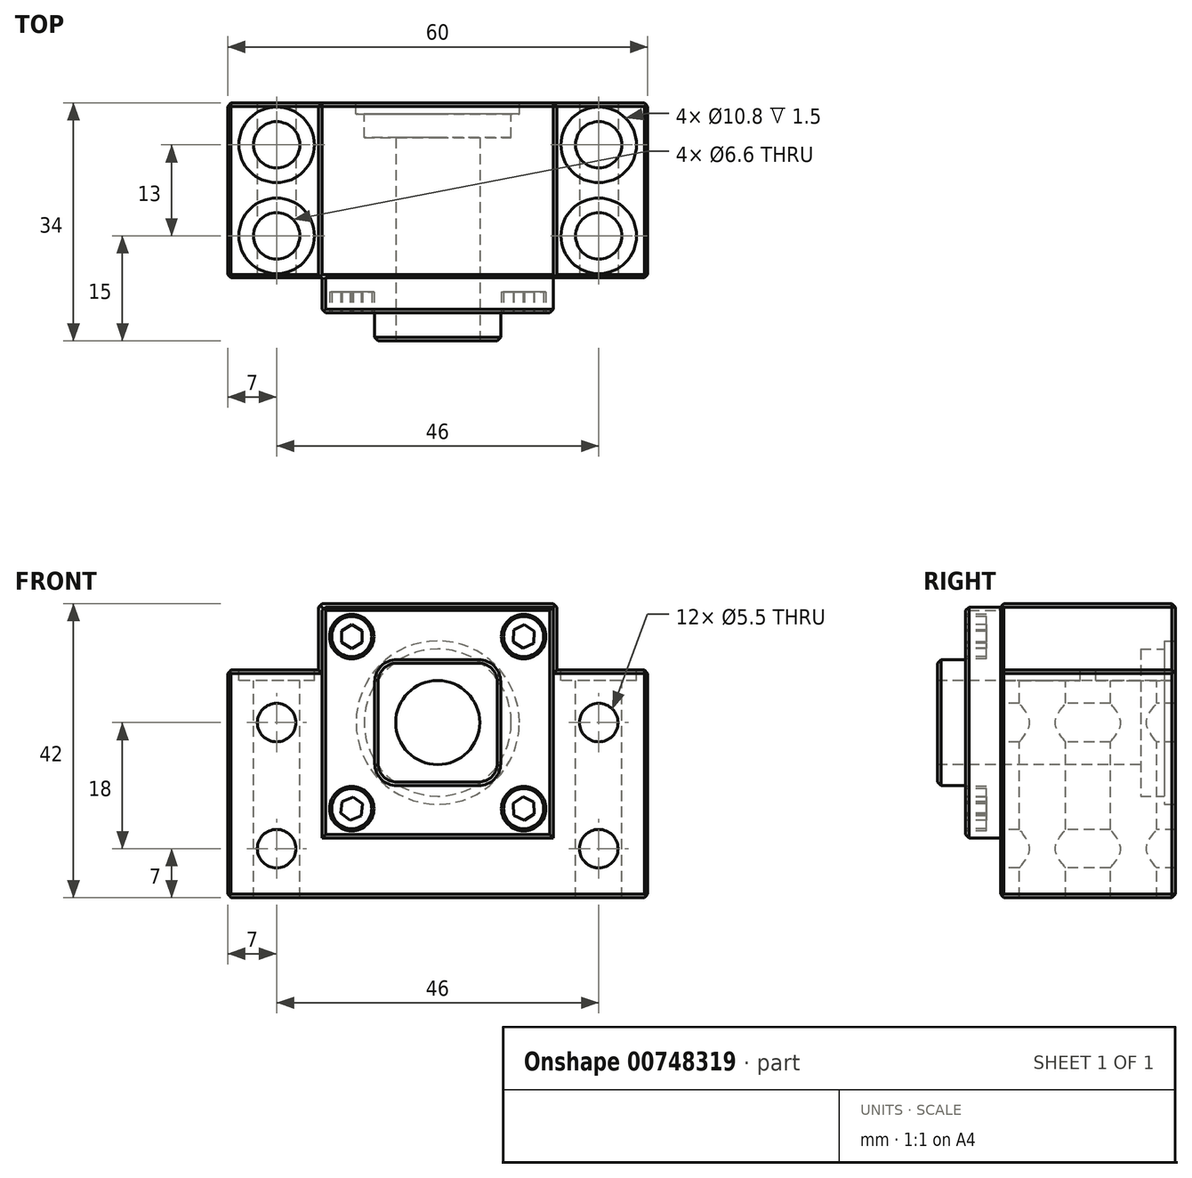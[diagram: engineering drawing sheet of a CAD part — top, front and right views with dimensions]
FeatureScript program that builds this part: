
annotation { "Feature Type Name" : "Feature", "Feature Type Description" : "" }
export const myFeature = defineFeature(function(context is Context, id is Id, definition is map)
    precondition{}
    {
        {
            var Q0;
            Q0=qCreatedBy(makeId("Front.planeOp"),FACE);
            var sketch = newSketch(context, id + "F0", { "sketchPlane" : qUnion([Q0])});
            skLineSegment(sketch, "E0.bottom", {"start": v(0, 0) * mm, "end": v(60, 0) * mm});
            skLineSegment(sketch, "E0.top", {"start": v(0, 32.5) * mm, "end": v(13, 32.5) * mm});
            skLineSegment(sketch, "E0.left", {"start": v(0, 0) * mm, "end": v(0, 32.5) * mm});
            skLineSegment(sketch, "E0.right", {"start": v(60, 0) * mm, "end": v(60, 32.5) * mm});
            skLineSegment(sketch, "E1", {"start": v(30, 32.5) * mm, "end": v(30, 0) * mm, "construction": true});
            skLineSegment(sketch, "E2", {"start": v(0, 25) * mm, "end": v(60, 25) * mm, "construction": true});
            skLineSegment(sketch, "E3.bottom", {"start": v(47, 42) * mm, "end": v(13, 42) * mm});
            skLineSegment(sketch, "E3.left", {"start": v(47, 42) * mm, "end": v(47, 32.5) * mm});
            skLineSegment(sketch, "E3.right", {"start": v(13, 42) * mm, "end": v(13, 32.5) * mm});
            skPoint(sketch, "E3.middle", {"position": v(30, 25) * mm});
            skLineSegment(sketch, "E4.trimOffspring", {"start": v(47, 32.5) * mm, "end": v(60, 32.5) * mm});
            skSolve(sketch);
        }
        {
            var Q0;
            Q0 = qSketchRegion(id + "F0", true);
            extrude(context, id + "F1", {"entities" : qUnion([Q0]), "depth" : 25 * mm, "offsetDistance" : 25.4 * mm});
        }
        {
            var Q0;
            Q0=makeQuery(id+"F1.opExtrude","CAP_FACE",FACE,{"disambiguationData":[OSD([sQuery(id+"F0.wireOp",EDGE,"E0.bottom"),sQuery(id+"F0.wireOp",EDGE,"E0.top"),sQuery(id+"F0.wireOp",EDGE,"E0.left"),sQuery(id+"F0.wireOp",EDGE,"E0.right"),sQuery(id+"F0.wireOp",EDGE,"E3.bottom"),sQuery(id+"F0.wireOp",EDGE,"E3.left"),sQuery(id+"F0.wireOp",EDGE,"E3.right"),sQuery(id+"F0.wireOp",EDGE,"E4.trimOffspring")])],"isStart":false});
            var sketch = newSketch(context, id + "F2", { "sketchPlane" : qUnion([Q0])});
            skLineSegment(sketch, "E5", {"start": v(30, 42) * mm, "end": v(30, 0) * mm, "construction": true});
            skLineSegment(sketch, "E6", {"start": v(0, 25) * mm, "end": v(60, 25) * mm, "construction": true});
            skPoint(sketch, "E7.middle", {"position": v(30, 25) * mm});
            skLineSegment(sketch, "E8.bottom", {"start": v(46.5, 41.5) * mm, "end": v(13.5, 41.5) * mm});
            skLineSegment(sketch, "E8.top", {"start": v(46.5, 8.5) * mm, "end": v(13.5, 8.5) * mm});
            skLineSegment(sketch, "E8.left", {"start": v(46.5, 41.5) * mm, "end": v(46.5, 8.5) * mm});
            skLineSegment(sketch, "E8.right", {"start": v(13.5, 41.5) * mm, "end": v(13.5, 8.5) * mm});
            skSolve(sketch);
        }
        {
            var Q0;
            Q0 = qSketchRegion(id + "F2", true);
            extrude(context, id + "F3", {"entities" : qUnion([Q0]), "operationType" : NewBodyOperationType.ADD, "depth" : 5 * mm, "offsetDistance" : 25.4 * mm});
        }
        {
            var Q0;
            Q0=makeQuery(id+"F3.opExtrude","CAP_FACE",FACE,{"disambiguationData":[OSD([sQuery(id+"F2.wireOp",EDGE,"E8.bottom"),sQuery(id+"F2.wireOp",EDGE,"E8.top"),sQuery(id+"F2.wireOp",EDGE,"E8.left"),sQuery(id+"F2.wireOp",EDGE,"E8.right")])],"isStart":false});
            var sketch = newSketch(context, id + "F4", { "sketchPlane" : qUnion([Q0])});
            skLineSegment(sketch, "E9.bottom", {"start": v(35.83, 34) * mm, "end": v(24.17, 34) * mm});
            skLineSegment(sketch, "E9.top", {"start": v(35.83, 16) * mm, "end": v(24.17, 16) * mm});
            skLineSegment(sketch, "E9.left", {"start": v(39, 30.83) * mm, "end": v(39, 19.17) * mm});
            skLineSegment(sketch, "E9.right", {"start": v(21, 30.83) * mm, "end": v(21, 19.17) * mm});
            skPoint(sketch, "E9.middle", {"position": v(30, 25) * mm});
            skPoint(sketch, "E9.middle.positionSnap0", {"position": v(46.5, 25) * mm});
            skPoint(sketch, "E9.middle.positionSnap1", {"position": v(30, 41.5) * mm});
            skPoint(sketch, "E9.centerSnap0", {"position": v(46.5, 25) * mm});
            skPoint(sketch, "E9.centerSnap1", {"position": v(30, 41.5) * mm});
            skPoint(sketch, "E10.visualSharp", {"position": v(21, 34) * mm});
            skArc(sketch, "E10.filletArc", {"start": v(24.17, 34) * mm, "mid": v(21.93, 33.07) * mm, "end": v(21, 30.83) * mm});
            skPoint(sketch, "E11.visualSharp", {"position": v(39, 34) * mm});
            skArc(sketch, "E11.filletArc", {"start": v(39, 30.83) * mm, "mid": v(38.07, 33.07) * mm, "end": v(35.83, 34) * mm});
            skPoint(sketch, "E12.visualSharp", {"position": v(39, 16) * mm});
            skArc(sketch, "E12.filletArc", {"start": v(35.83, 16) * mm, "mid": v(38.07, 16.93) * mm, "end": v(39, 19.17) * mm});
            skPoint(sketch, "E13.visualSharp", {"position": v(21, 16) * mm});
            skArc(sketch, "E13.filletArc", {"start": v(21, 19.17) * mm, "mid": v(21.93, 16.93) * mm, "end": v(24.17, 16) * mm});
            skSolve(sketch);
        }
        {
            var Q0;
            Q0 = qSketchRegion(id + "F4", true);
            extrude(context, id + "F5", {"entities" : qUnion([Q0]), "operationType" : NewBodyOperationType.ADD, "depth" : 4 * mm, "offsetDistance" : 25.4 * mm});
        }
        {
            var Q0;
            Q0=makeQuery(id+"F5.opExtrude","CAP_FACE",FACE,{"disambiguationData":[OSD([sQuery(id+"F4.wireOp",EDGE,"E9.bottom"),sQuery(id+"F4.wireOp",EDGE,"E9.top"),sQuery(id+"F4.wireOp",EDGE,"E9.left"),sQuery(id+"F4.wireOp",EDGE,"E9.right"),sQuery(id+"F4.wireOp",EDGE,"E10.filletArc"),sQuery(id+"F4.wireOp",EDGE,"E11.filletArc"),sQuery(id+"F4.wireOp",EDGE,"E12.filletArc"),sQuery(id+"F4.wireOp",EDGE,"E13.filletArc")])],"isStart":false});
            var sketch = newSketch(context, id + "F6", { "sketchPlane" : qUnion([Q0])});
            skCircle(sketch, "E14", {"center": v(30, 25) * mm, "radius": 6 * mm});
            skPoint(sketch, "E14.centerSnap0", {"position": v(39, 25) * mm});
            skPoint(sketch, "E14.centerSnap1", {"position": v(30, 34) * mm});
            skSolve(sketch);
        }
        {
            var Q0;
            Q0 = qSketchRegion(id + "F6", true);
            extrude(context, id + "F7", {"entities" : qUnion([Q0]), "operationType" : NewBodyOperationType.REMOVE, "endBound" : BoundingType.THROUGH_ALL, "oppositeDirection" : true, "depth" : 25.4 * mm, "offsetDistance" : 25.4 * mm});
        }
        {
            var Q0;
            Q0=makeQuery(id+"F1.opExtrude","CAP_FACE",FACE,{"disambiguationData":[OSD([sQuery(id+"F0.wireOp",EDGE,"E0.bottom"),sQuery(id+"F0.wireOp",EDGE,"E0.top"),sQuery(id+"F0.wireOp",EDGE,"E0.left"),sQuery(id+"F0.wireOp",EDGE,"E0.right"),sQuery(id+"F0.wireOp",EDGE,"E3.bottom"),sQuery(id+"F0.wireOp",EDGE,"E3.left"),sQuery(id+"F0.wireOp",EDGE,"E3.right"),sQuery(id+"F0.wireOp",EDGE,"E4.trimOffspring")])],"isStart":false});
            var sketch = newSketch(context, id + "F8", { "sketchPlane" : qUnion([Q0])});
            skLineSegment(sketch, "E15", {"start": v(0, 25) * mm, "end": v(60, 25) * mm, "construction": true});
            skLineSegment(sketch, "E16", {"start": v(30, 25) * mm, "end": v(30, 0) * mm, "construction": true});
            skLineSegment(sketch, "E17.0", {"start": v(7, 25) * mm, "end": v(7, 0) * mm, "construction": true});
            skLineSegment(sketch, "E18.0", {"start": v(53, 25) * mm, "end": v(53, 0) * mm, "construction": true});
            skLineSegment(sketch, "E19", {"start": v(7, 7) * mm, "end": v(53, 7) * mm, "construction": true});
            skCircle(sketch, "E20", {"center": v(7, 25) * mm, "radius": 2.75 * mm});
            skCircle(sketch, "E21", {"center": v(7, 7) * mm, "radius": 2.75 * mm});
            skCircle(sketch, "E22", {"center": v(53, 25) * mm, "radius": 2.75 * mm});
            skCircle(sketch, "E23", {"center": v(53, 7) * mm, "radius": 2.75 * mm});
            skSolve(sketch);
        }
        {
            var Q0;
            Q0 = qSketchRegion(id + "F8", true);
            extrude(context, id + "F9", {"entities" : qUnion([Q0]), "operationType" : NewBodyOperationType.REMOVE, "endBound" : BoundingType.THROUGH_ALL, "oppositeDirection" : true, "depth" : 25.4 * mm, "offsetDistance" : 25.4 * mm});
        }
        {
            var Q0;
            Q0=makeQuery(id+"F1.opExtrude","SWEPT_FACE",FACE,{"disambiguationData":[OSD([sQuery(id+"F0.wireOp",EDGE,"E4.trimOffspring")])]});
            var sketch = newSketch(context, id + "F10", { "sketchPlane" : qUnion([Q0])});
            skLineSegment(sketch, "E24", {"start": v(60, -12.5) * mm, "end": v(0, -12.5) * mm, "construction": true});
            skLineSegment(sketch, "E25.0", {"start": v(60, -6) * mm, "end": v(0, -6) * mm, "construction": true});
            skLineSegment(sketch, "E26.0", {"start": v(60, -19) * mm, "end": v(0, -19) * mm, "construction": true});
            skLineSegment(sketch, "E27", {"start": v(30, -6) * mm, "end": v(30, -19) * mm, "construction": true});
            skLineSegment(sketch, "E28.0", {"start": v(7, -6) * mm, "end": v(7, -19) * mm, "construction": true});
            skLineSegment(sketch, "E29.0", {"start": v(53, -6) * mm, "end": v(53, -19) * mm, "construction": true});
            skCircle(sketch, "E30", {"center": v(7, -6) * mm, "radius": 5.4 * mm});
            skCircle(sketch, "E31", {"center": v(7, -19) * mm, "radius": 5.4 * mm});
            skCircle(sketch, "E32", {"center": v(53, -6) * mm, "radius": 5.4 * mm});
            skCircle(sketch, "E33", {"center": v(53, -19) * mm, "radius": 5.4 * mm});
            skSolve(sketch);
        }
        {
            var Q0;
            Q0 = qSketchRegion(id + "F10", true);
            extrude(context, id + "F11", {"entities" : qUnion([Q0]), "operationType" : NewBodyOperationType.REMOVE, "oppositeDirection" : true, "depth" : 1.5 * mm, "offsetDistance" : 25.4 * mm});
        }
        {
            var Q0;
            Q0=makeQuery(id+"F11.boolean.opBoolean","COPY",FACE,{"derivedFrom":makeQuery(id+"F11.opExtrude","CAP_FACE",FACE,{"disambiguationData":[OSD([sQuery(id+"F10.wireOp",EDGE,"E30")])],"isStart":false})});
            var sketch = newSketch(context, id + "F12", { "sketchPlane" : qUnion([Q0])});
            skCircle(sketch, "E34", {"center": v(7, -6) * mm, "radius": 3.3 * mm});
            skLineSegment(sketch, "E35", {"start": v(7, -6) * mm, "end": v(53, -6) * mm, "construction": true});
            skLineSegment(sketch, "E36", {"start": v(53, -6) * mm, "end": v(53, -19) * mm, "construction": true});
            skLineSegment(sketch, "E37", {"start": v(53, -19) * mm, "end": v(7, -19) * mm, "construction": true});
            skCircle(sketch, "E38", {"center": v(53, -6) * mm, "radius": 3.3 * mm});
            skCircle(sketch, "E39", {"center": v(53, -19) * mm, "radius": 3.3 * mm});
            skCircle(sketch, "E40", {"center": v(7, -19) * mm, "radius": 3.3 * mm});
            skSolve(sketch);
        }
        {
            var Q0;
            Q0 = qSketchRegion(id + "F12", true);
            extrude(context, id + "F13", {"entities" : qUnion([Q0]), "operationType" : NewBodyOperationType.REMOVE, "endBound" : BoundingType.THROUGH_ALL, "oppositeDirection" : true, "depth" : 25.4 * mm, "offsetDistance" : 25.4 * mm});
        }
        {
            var Q0;
            Q0=makeQuery(id+"F3.opExtrude","CAP_FACE",FACE,{"disambiguationData":[OSD([sQuery(id+"F2.wireOp",EDGE,"E8.bottom"),sQuery(id+"F2.wireOp",EDGE,"E8.top"),sQuery(id+"F2.wireOp",EDGE,"E8.left"),sQuery(id+"F2.wireOp",EDGE,"E8.right")])],"isStart":false});
            var sketch = newSketch(context, id + "F14", { "sketchPlane" : qUnion([Q0])});
            skLineSegment(sketch, "E41", {"start": v(21.93, 33.07) * mm, "end": v(13.5, 41.5) * mm, "construction": true});
            skLineSegment(sketch, "E42", {"start": v(38.07, 33.07) * mm, "end": v(46.5, 41.5) * mm, "construction": true});
            skLineSegment(sketch, "E43", {"start": v(38.07, 16.93) * mm, "end": v(46.5, 8.5) * mm, "construction": true});
            skLineSegment(sketch, "E44", {"start": v(21.93, 16.93) * mm, "end": v(13.5, 8.5) * mm, "construction": true});
            skCircle(sketch, "E45", {"center": v(17.71, 37.29) * mm, "radius": 3.18 * mm});
            skCircle(sketch, "E46", {"center": v(42.29, 37.29) * mm, "radius": 3.18 * mm});
            skCircle(sketch, "E47", {"center": v(42.29, 12.71) * mm, "radius": 3.18 * mm});
            skCircle(sketch, "E48", {"center": v(17.71, 12.71) * mm, "radius": 3.18 * mm});
            skCircle(sketch, "E49", {"center": v(17.71, 37.29) * mm, "radius": 2.86 * mm});
            skCircle(sketch, "E50", {"center": v(42.29, 37.29) * mm, "radius": 2.86 * mm});
            skCircle(sketch, "E51", {"center": v(42.29, 12.71) * mm, "radius": 2.86 * mm});
            skCircle(sketch, "E52", {"center": v(17.71, 12.71) * mm, "radius": 2.86 * mm});
            skLineSegment(sketch, "E53.0", {"start": v(19.18, 38.13) * mm, "end": v(19.18, 36.44) * mm});
            skLineSegment(sketch, "E53.1", {"start": v(19.18, 36.44) * mm, "end": v(17.71, 35.6) * mm});
            skLineSegment(sketch, "E53.2", {"start": v(17.71, 35.6) * mm, "end": v(16.25, 36.44) * mm});
            skLineSegment(sketch, "E53.3", {"start": v(16.25, 36.44) * mm, "end": v(16.25, 38.13) * mm});
            skLineSegment(sketch, "E53.4", {"start": v(16.25, 38.13) * mm, "end": v(17.71, 38.97) * mm});
            skLineSegment(sketch, "E53.5", {"start": v(17.71, 38.97) * mm, "end": v(19.18, 38.13) * mm});
            skPoint(sketch, "E53.0.midPoint", {"position": v(19.18, 37.29) * mm});
            skLineSegment(sketch, "E54.0", {"start": v(43.8, 38.04) * mm, "end": v(43.7, 36.36) * mm});
            skLineSegment(sketch, "E54.1", {"start": v(43.7, 36.36) * mm, "end": v(42.18, 35.6) * mm});
            skLineSegment(sketch, "E54.2", {"start": v(42.18, 35.6) * mm, "end": v(40.78, 36.53) * mm});
            skLineSegment(sketch, "E54.3", {"start": v(40.78, 36.53) * mm, "end": v(40.88, 38.21) * mm});
            skLineSegment(sketch, "E54.4", {"start": v(40.88, 38.21) * mm, "end": v(42.39, 38.97) * mm});
            skLineSegment(sketch, "E54.5", {"start": v(42.39, 38.97) * mm, "end": v(43.8, 38.04) * mm});
            skPoint(sketch, "E54.0.midPoint", {"position": v(43.74, 37.2) * mm});
            skLineSegment(sketch, "E55.0", {"start": v(43.7, 13.64) * mm, "end": v(43.8, 11.96) * mm});
            skLineSegment(sketch, "E55.1", {"start": v(43.8, 11.96) * mm, "end": v(42.39, 11.03) * mm});
            skLineSegment(sketch, "E55.2", {"start": v(42.39, 11.03) * mm, "end": v(40.88, 11.79) * mm});
            skLineSegment(sketch, "E55.3", {"start": v(40.88, 11.79) * mm, "end": v(40.78, 13.47) * mm});
            skLineSegment(sketch, "E55.4", {"start": v(40.78, 13.47) * mm, "end": v(42.18, 14.4) * mm});
            skLineSegment(sketch, "E55.5", {"start": v(42.18, 14.4) * mm, "end": v(43.7, 13.64) * mm});
            skPoint(sketch, "E55.0.midPoint", {"position": v(43.74, 12.8) * mm});
            skLineSegment(sketch, "E56.0", {"start": v(19.26, 13.38) * mm, "end": v(19.07, 11.7) * mm});
            skLineSegment(sketch, "E56.1", {"start": v(19.07, 11.7) * mm, "end": v(17.52, 11.04) * mm});
            skLineSegment(sketch, "E56.2", {"start": v(17.52, 11.04) * mm, "end": v(16.17, 12.05) * mm});
            skLineSegment(sketch, "E56.3", {"start": v(16.17, 12.05) * mm, "end": v(16.36, 13.72) * mm});
            skLineSegment(sketch, "E56.4", {"start": v(16.36, 13.72) * mm, "end": v(17.91, 14.39) * mm});
            skLineSegment(sketch, "E56.5", {"start": v(17.91, 14.39) * mm, "end": v(19.26, 13.38) * mm});
            skPoint(sketch, "E56.0.midPoint", {"position": v(19.17, 12.55) * mm});
            skSolve(sketch);
        }
        {
            var Q0;
            Q0=makeQuery(id+"F14.imprint","IMPRINT",FACE,{"disambiguationData":[TD([[makeQuery(id+"F14.imprint","IMPRINT",EDGE,{"derivedFrom":sQuery(id+"F14.wireOp",EDGE,"E53.0")}),-1.0]])]});
            var Q1;
            Q1=makeQuery(id+"F14.imprint","IMPRINT",FACE,{"disambiguationData":[TD([[makeQuery(id+"F14.imprint","IMPRINT",EDGE,{"derivedFrom":sQuery(id+"F14.wireOp",EDGE,"E45")}),1.0]])]});
            var Q2;
            Q2=makeQuery(id+"F14.imprint","IMPRINT",FACE,{"disambiguationData":[TD([[makeQuery(id+"F14.imprint","IMPRINT",EDGE,{"derivedFrom":sQuery(id+"F14.wireOp",EDGE,"E54.0")}),-1.0]])]});
            var Q3;
            Q3=makeQuery(id+"F14.imprint","IMPRINT",FACE,{"disambiguationData":[TD([[makeQuery(id+"F14.imprint","IMPRINT",EDGE,{"derivedFrom":sQuery(id+"F14.wireOp",EDGE,"E46")}),1.0]])]});
            var Q4;
            Q4=makeQuery(id+"F14.imprint","IMPRINT",FACE,{"disambiguationData":[TD([[makeQuery(id+"F14.imprint","IMPRINT",EDGE,{"derivedFrom":sQuery(id+"F14.wireOp",EDGE,"E55.0")}),-1.0]])]});
            var Q5;
            Q5=makeQuery(id+"F14.imprint","IMPRINT",FACE,{"disambiguationData":[TD([[makeQuery(id+"F14.imprint","IMPRINT",EDGE,{"derivedFrom":sQuery(id+"F14.wireOp",EDGE,"E47")}),1.0]])]});
            var Q6;
            Q6=makeQuery(id+"F14.imprint","IMPRINT",FACE,{"disambiguationData":[TD([[makeQuery(id+"F14.imprint","IMPRINT",EDGE,{"derivedFrom":sQuery(id+"F14.wireOp",EDGE,"E56.0")}),-1.0]])]});
            var Q7;
            Q7=makeQuery(id+"F14.imprint","IMPRINT",FACE,{"disambiguationData":[TD([[makeQuery(id+"F14.imprint","IMPRINT",EDGE,{"derivedFrom":sQuery(id+"F14.wireOp",EDGE,"E48")}),1.0]])]});
            extrude(context, id + "F15", {"entities" : qUnion([Q0, Q1, Q2, Q3, Q4, Q5, Q6, Q7]), "operationType" : NewBodyOperationType.REMOVE, "oppositeDirection" : true, "depth" : 3 * mm, "offsetDistance" : 25.4 * mm});
        }
        {
            var Q0;
            Q0=makeQuery(id+"F1.opExtrude","CAP_FACE",FACE,{"disambiguationData":[OSD([sQuery(id+"F0.wireOp",EDGE,"E0.bottom"),sQuery(id+"F0.wireOp",EDGE,"E0.top"),sQuery(id+"F0.wireOp",EDGE,"E0.left"),sQuery(id+"F0.wireOp",EDGE,"E0.right"),sQuery(id+"F0.wireOp",EDGE,"E3.bottom"),sQuery(id+"F0.wireOp",EDGE,"E3.left"),sQuery(id+"F0.wireOp",EDGE,"E3.right"),sQuery(id+"F0.wireOp",EDGE,"E4.trimOffspring")])],"isStart":true});
            var sketch = newSketch(context, id + "F16", { "sketchPlane" : qUnion([Q0])});
            skCircle(sketch, "E57", {"center": v(-30, 25) * mm, "radius": 10.5 * mm});
            skSolve(sketch);
        }
        {
            var Q0;
            Q0 = qSketchRegion(id + "F16", true);
            extrude(context, id + "F17", {"entities" : qUnion([Q0]), "operationType" : NewBodyOperationType.REMOVE, "oppositeDirection" : true, "depth" : 5 * mm, "offsetDistance" : 25.4 * mm});
        }
        {
            var Q0;
            Q0=makeQuery(id+"F1.opExtrude","CAP_FACE",FACE,{"disambiguationData":[OSD([sQuery(id+"F0.wireOp",EDGE,"E0.bottom"),sQuery(id+"F0.wireOp",EDGE,"E0.top"),sQuery(id+"F0.wireOp",EDGE,"E0.left"),sQuery(id+"F0.wireOp",EDGE,"E0.right"),sQuery(id+"F0.wireOp",EDGE,"E3.bottom"),sQuery(id+"F0.wireOp",EDGE,"E3.left"),sQuery(id+"F0.wireOp",EDGE,"E3.right"),sQuery(id+"F0.wireOp",EDGE,"E4.trimOffspring")])],"isStart":true});
            var sketch = newSketch(context, id + "F18", { "sketchPlane" : qUnion([Q0])});
            skCircle(sketch, "E58", {"center": v(-30, 25) * mm, "radius": 11.66 * mm});
            skSolve(sketch);
        }
        {
            var Q0;
            Q0 = qSketchRegion(id + "F18", true);
            extrude(context, id + "F19", {"entities" : qUnion([Q0]), "operationType" : NewBodyOperationType.REMOVE, "oppositeDirection" : true, "depth" : 1.6 * mm, "offsetDistance" : 25.4 * mm});
        }
        {
            var Q0;
            Q0=makeQuery(id+"F3.opExtrude","CAP_EDGE",EDGE,{"disambiguationData":[OSD([sQuery(id+"F2.wireOp",EDGE,"E8.right")])],"isStart":false});
            var Q1;
            Q1=makeQuery(id+"F3.opExtrude","CAP_EDGE",EDGE,{"disambiguationData":[OSD([sQuery(id+"F2.wireOp",EDGE,"E8.bottom")])],"isStart":false});
            var Q2;
            Q2=makeQuery(id+"F3.opExtrude","CAP_EDGE",EDGE,{"disambiguationData":[OSD([sQuery(id+"F2.wireOp",EDGE,"E8.left")])],"isStart":false});
            var Q3;
            Q3=makeQuery(id+"F3.opExtrude","CAP_EDGE",EDGE,{"disambiguationData":[OSD([sQuery(id+"F2.wireOp",EDGE,"E8.top")])],"isStart":false});
            var Q4;
            Q4=makeQuery(id+"F5.opExtrude","CAP_EDGE",EDGE,{"disambiguationData":[OSD([sQuery(id+"F4.wireOp",EDGE,"E9.right")])],"isStart":false});
            chamfer(context, id + "F20", {"entities" : qUnion([Q0, Q1, Q2, Q3, Q4]), "width" : .5 * mm, "tangentPropagation" : true});
        }
        {
            var Q0;
            Q0=makeQuery(id+"F1.opExtrude","CAP_EDGE",EDGE,{"disambiguationData":[OSD([sQuery(id+"F0.wireOp",EDGE,"E3.right")])],"isStart":false});
            var Q1;
            Q1=makeQuery(id+"F1.opExtrude","CAP_EDGE",EDGE,{"disambiguationData":[OSD([sQuery(id+"F0.wireOp",EDGE,"E3.bottom")])],"isStart":false});
            var Q2;
            Q2=makeQuery(id+"F1.opExtrude","CAP_EDGE",EDGE,{"disambiguationData":[OSD([sQuery(id+"F0.wireOp",EDGE,"E3.left")])],"isStart":false});
            var Q3;
            Q3=makeQuery(id+"F1.opExtrude","CAP_EDGE",EDGE,{"disambiguationData":[OSD([sQuery(id+"F0.wireOp",EDGE,"E4.trimOffspring")])],"isStart":false});
            var Q4;
            Q4=makeQuery(id+"F1.opExtrude","SWEPT_EDGE",EDGE,{"disambiguationData":[OSD([sQuery(id+"F0.wireOp",EDGE,"E0.right"),sQuery(id+"F0.wireOp",EDGE,"E4.trimOffspring")])]});
            var Q5;
            Q5=makeQuery(id+"F1.opExtrude","CAP_EDGE",EDGE,{"disambiguationData":[OSD([sQuery(id+"F0.wireOp",EDGE,"E0.right")])],"isStart":false});
            var Q6;
            Q6=makeQuery(id+"F1.opExtrude","CAP_EDGE",EDGE,{"disambiguationData":[OSD([sQuery(id+"F0.wireOp",EDGE,"E0.bottom")])],"isStart":false});
            var Q7;
            Q7=makeQuery(id+"F1.opExtrude","CAP_EDGE",EDGE,{"disambiguationData":[OSD([sQuery(id+"F0.wireOp",EDGE,"E0.left")])],"isStart":false});
            var Q8;
            Q8=makeQuery(id+"F1.opExtrude","CAP_EDGE",EDGE,{"disambiguationData":[OSD([sQuery(id+"F0.wireOp",EDGE,"E0.top")])],"isStart":false});
            chamfer(context, id + "F21", {"entities" : qUnion([Q0, Q1, Q2, Q3, Q4, Q5, Q6, Q7, Q8]), "width" : .5 * mm, "tangentPropagation" : true});
        }
        {
            var Q0;
            Q0=makeQuery(id+"F3.opExtrude","SWEPT_EDGE",EDGE,{"disambiguationData":[OSD([sQuery(id+"F2.wireOp",EDGE,"E8.bottom"),sQuery(id+"F2.wireOp",EDGE,"E8.right")])]});
            var Q1;
            Q1=makeQuery(id+"F1.opExtrude","SWEPT_EDGE",EDGE,{"disambiguationData":[OSD([sQuery(id+"F0.wireOp",EDGE,"E3.bottom"),sQuery(id+"F0.wireOp",EDGE,"E3.right")])]});
            var Q2;
            Q2=makeQuery(id+"F1.opExtrude","SWEPT_EDGE",EDGE,{"disambiguationData":[OSD([sQuery(id+"F0.wireOp",EDGE,"E0.top"),sQuery(id+"F0.wireOp",EDGE,"E0.left")])]});
            var Q3;
            Q3=makeQuery(id+"F1.opExtrude","SWEPT_EDGE",EDGE,{"disambiguationData":[OSD([sQuery(id+"F0.wireOp",EDGE,"E0.bottom"),sQuery(id+"F0.wireOp",EDGE,"E0.left")])]});
            var Q4;
            Q4=makeQuery(id+"F1.opExtrude","SWEPT_EDGE",EDGE,{"disambiguationData":[OSD([sQuery(id+"F0.wireOp",EDGE,"E0.bottom"),sQuery(id+"F0.wireOp",EDGE,"E0.right")])]});
            var Q5;
            Q5=makeQuery(id+"F1.opExtrude","SWEPT_EDGE",EDGE,{"disambiguationData":[OSD([sQuery(id+"F0.wireOp",EDGE,"E3.bottom"),sQuery(id+"F0.wireOp",EDGE,"E3.left")])]});
            var Q6;
            Q6=makeQuery(id+"F1.opExtrude","CAP_EDGE",EDGE,{"disambiguationData":[OSD([sQuery(id+"F0.wireOp",EDGE,"E3.bottom")])],"isStart":true});
            var Q7;
            Q7=makeQuery(id+"F1.opExtrude","CAP_EDGE",EDGE,{"disambiguationData":[OSD([sQuery(id+"F0.wireOp",EDGE,"E3.left")])],"isStart":true});
            var Q8;
            Q8=makeQuery(id+"F1.opExtrude","CAP_EDGE",EDGE,{"disambiguationData":[OSD([sQuery(id+"F0.wireOp",EDGE,"E4.trimOffspring")])],"isStart":true});
            var Q9;
            Q9=makeQuery(id+"F1.opExtrude","CAP_EDGE",EDGE,{"disambiguationData":[OSD([sQuery(id+"F0.wireOp",EDGE,"E0.right")])],"isStart":true});
            var Q10;
            Q10=makeQuery(id+"F1.opExtrude","CAP_EDGE",EDGE,{"disambiguationData":[OSD([sQuery(id+"F0.wireOp",EDGE,"E0.bottom")])],"isStart":true});
            var Q11;
            Q11=makeQuery(id+"F1.opExtrude","CAP_EDGE",EDGE,{"disambiguationData":[OSD([sQuery(id+"F0.wireOp",EDGE,"E0.left")])],"isStart":true});
            var Q12;
            Q12=makeQuery(id+"F1.opExtrude","CAP_EDGE",EDGE,{"disambiguationData":[OSD([sQuery(id+"F0.wireOp",EDGE,"E0.top")])],"isStart":true});
            var Q13;
            Q13=makeQuery(id+"F1.opExtrude","CAP_EDGE",EDGE,{"disambiguationData":[OSD([sQuery(id+"F0.wireOp",EDGE,"E3.right")])],"isStart":true});
            chamfer(context, id + "F22", {"entities" : qUnion([Q0, Q1, Q2, Q3, Q4, Q5, Q6, Q7, Q8, Q9, Q10, Q11, Q12, Q13]), "width" : .5 * mm, "tangentPropagation" : true});
        }
    });
